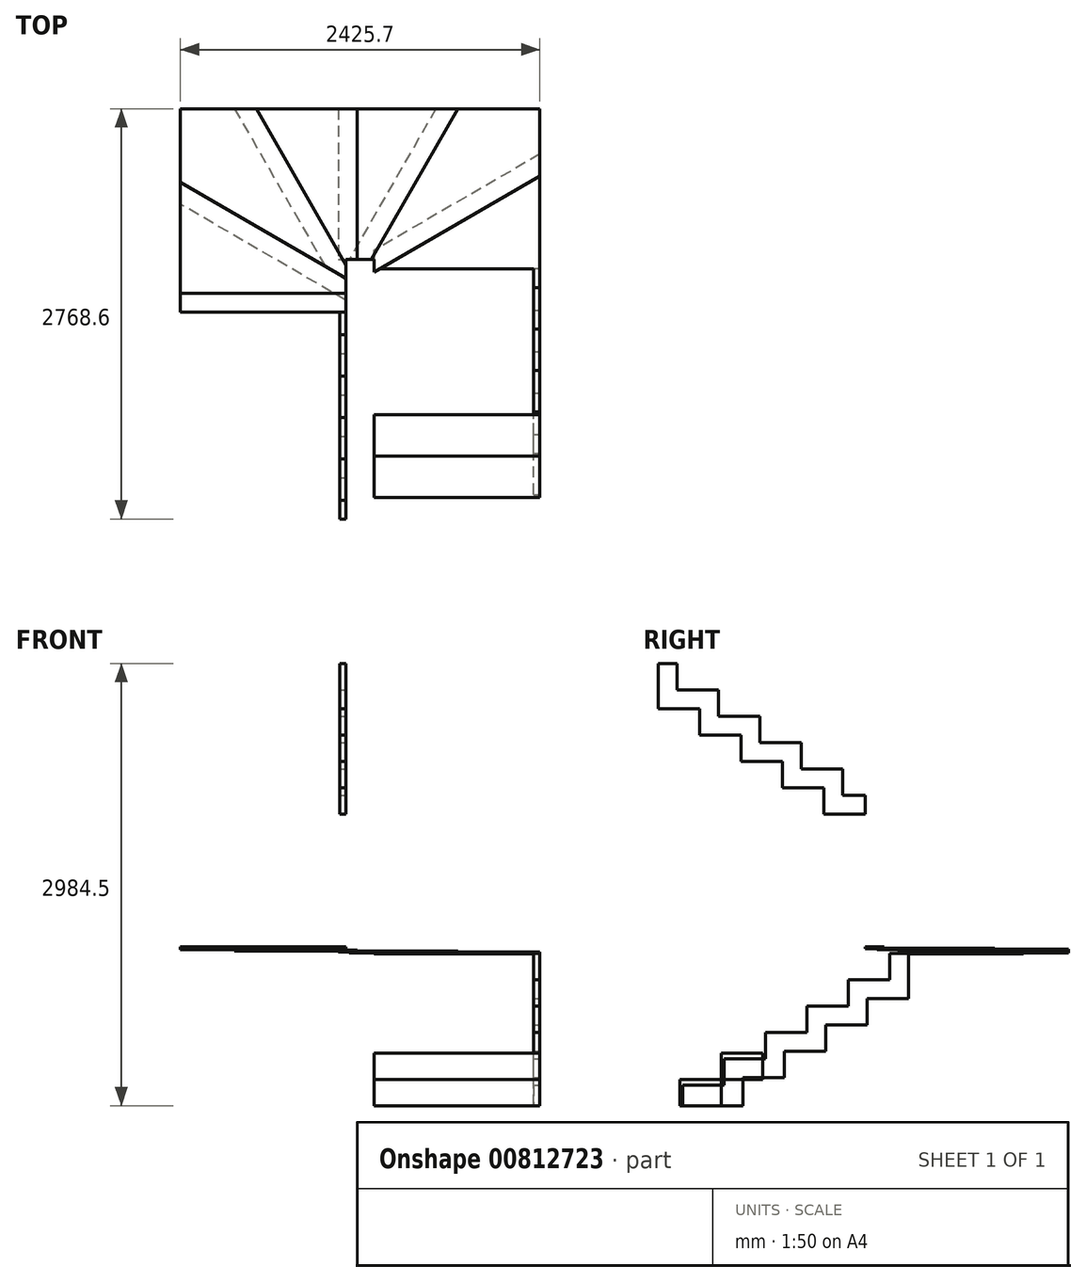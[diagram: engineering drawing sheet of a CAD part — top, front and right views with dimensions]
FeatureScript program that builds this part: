
annotation { "Feature Type Name" : "Feature", "Feature Type Description" : "" }
export const myFeature = defineFeature(function(context is Context, id is Id, definition is map)
    precondition{}
    {
        {
            assignVariable(context, id + "F0", {"name" : "ancho", "anyValue" : 44});
        }
        {
            assignVariable(context, id + "F1", {"name" : "ch", "anyValue" : 7});
        }
        {
            assignVariable(context, id + "F2", {"name" : "tk", "anyValue" : 5});
        }
        {
            var Q0;
            Q0=qCreatedBy(makeId("Top.planeOp"),FACE);
            var sketch = newSketch(context, id + "F3", { "sketchPlane" : qUnion([Q0])});
            skCircle(sketch, "E0", {"center": v(0, 0) * mm, "radius": 1212.85 * mm, "construction": true});
            skLineSegment(sketch, "E1", {"start": v(0, 0) * mm, "end": v(-1212.85, 0) * mm, "construction": true});
            skLineSegment(sketch, "E2", {"start": v(0, 0) * mm, "end": v(1212.85, 0) * mm, "construction": true});
            skLineSegment(sketch, "E3", {"start": v(0, 0) * mm, "end": v(0, 1212.85) * mm, "construction": true});
            skLineSegment(sketch, "E4.bottom", {"start": v(95.25, 1323.25) * mm, "end": v(-95.25, 1323.25) * mm, "construction": true});
            skLineSegment(sketch, "E4.top", {"start": v(95.25, -3517.78) * mm, "end": v(-95.25, -3517.78) * mm, "construction": true});
            skLineSegment(sketch, "E4.left", {"start": v(95.25, 1323.25) * mm, "end": v(95.25, -3517.78) * mm, "construction": true});
            skLineSegment(sketch, "E4.right", {"start": v(-95.25, 1323.25) * mm, "end": v(-95.25, -3517.78) * mm, "construction": true});
            skLineSegment(sketch, "E5", {"start": v(-190.5, 1323.25) * mm, "end": v(-190.5, -3534.77) * mm, "construction": true});
            skLineSegment(sketch, "E6.bottom", {"start": v(-95.25, 0) * mm, "end": v(-1212.85, 0) * mm});
            skLineSegment(sketch, "E6.top", {"start": v(-95.25, -279.4) * mm, "end": v(-1212.85, -279.4) * mm});
            skLineSegment(sketch, "E6.left", {"start": v(-95.25, 0) * mm, "end": v(-95.25, -279.4) * mm});
            skLineSegment(sketch, "E6.right", {"start": v(-1212.85, 0) * mm, "end": v(-1212.85, -279.4) * mm});
            skLineSegment(sketch, "E7", {"start": v(-1212.85, 742.65) * mm, "end": v(73.46, 0) * mm, "construction": true});
            skLineSegment(sketch, "E8", {"start": v(-740.5, 1323.25) * mm, "end": v(623.95, -1040.04) * mm, "construction": true});
            skPoint(sketch, "E9", {"position": v(-190.5, 152.4) * mm});
            skPoint(sketch, "E10", {"position": v(-153.9, 307.25) * mm});
            skLineSegment(sketch, "E11", {"start": v(-153.9, 307.25) * mm, "end": v(0, 307.25) * mm, "construction": true});
            skPoint(sketch, "E12", {"position": v(0, 205.65) * mm});
            skLineSegment(sketch, "E13", {"start": v(0, 205.65) * mm, "end": v(-95.25, 205.65) * mm});
            skPoint(sketch, "E14", {"position": v(-95.25, 205.65) * mm});
            skPoint(sketch, "E15", {"position": v(-95.25, 97.4) * mm});
            skLineSegment(sketch, "E16", {"start": v(-95.25, 0) * mm, "end": v(-95.25, 97.4) * mm});
            skLineSegment(sketch, "E17", {"start": v(-1212.85, 742.65) * mm, "end": v(-1212.85, 0) * mm});
            skLineSegment(sketch, "E18", {"start": v(-1212.85, 742.65) * mm, "end": v(-95.25, 97.4) * mm});
            skLineSegment(sketch, "E19", {"start": v(-95.25, 97.4) * mm, "end": v(-95.25, 205.65) * mm});
            skLineSegment(sketch, "E20", {"start": v(0, 205.65) * mm, "end": v(0, 1323.25) * mm});
            skLineSegment(sketch, "E21", {"start": v(0, 1323.25) * mm, "end": v(-1212.85, 1323.25) * mm});
            skPoint(sketch, "E22", {"position": v(-740.5, 1323.25) * mm});
            skLineSegment(sketch, "E23", {"start": v(-95.25, 205.65) * mm, "end": v(-740.5, 1323.25) * mm});
            skLineSegment(sketch, "E24", {"start": v(-1212.85, 1323.25) * mm, "end": v(-1212.85, 742.65) * mm});
            skSolve(sketch);
        }
        {
            var Q0;
            Q0=qCreatedBy(makeId("Top.planeOp"),FACE);
            var sketch = newSketch(context, id + "F4", { "sketchPlane" : qUnion([Q0])});
            skLineSegment(sketch, "E25.bottom", {"start": v(95.25, 0) * mm, "end": v(1212.85, 0) * mm});
            skLineSegment(sketch, "E25.top", {"start": v(95.25, -279.4) * mm, "end": v(1212.85, -279.4) * mm});
            skLineSegment(sketch, "E25.left", {"start": v(95.25, 0) * mm, "end": v(95.25, -279.4) * mm});
            skLineSegment(sketch, "E25.right", {"start": v(1212.85, 0) * mm, "end": v(1212.85, -279.4) * mm});
            skLineSegment(sketch, "E26", {"start": v(95.25, 0) * mm, "end": v(95.25, 101.6) * mm});
            skLineSegment(sketch, "E27", {"start": v(95.25, 101.6) * mm, "end": v(1212.85, 749.3) * mm});
            skLineSegment(sketch, "E28", {"start": v(1212.85, 749.3) * mm, "end": v(1212.85, 0) * mm});
            skLineSegment(sketch, "E29", {"start": v(190.5, 0) * mm, "end": v(190.5, 156.8) * mm, "construction": true});
            skLineSegment(sketch, "E30", {"start": v(0, 209.55) * mm, "end": v(95.25, 209.55) * mm});
            skLineSegment(sketch, "E31", {"start": v(95.25, 209.55) * mm, "end": v(679.45, 1225.55) * mm});
            skLineSegment(sketch, "E32", {"start": v(679.45, 1225.55) * mm, "end": v(0, 1225.55) * mm});
            skLineSegment(sketch, "E33", {"start": v(0, 1225.55) * mm, "end": v(0, 209.55) * mm});
            skLineSegment(sketch, "E34", {"start": v(679.45, 1225.55) * mm, "end": v(1212.85, 1225.55) * mm});
            skLineSegment(sketch, "E35", {"start": v(1212.85, 1225.55) * mm, "end": v(1212.85, 749.3) * mm});
            skLineSegment(sketch, "E36", {"start": v(0, 304.8) * mm, "end": v(150.02, 304.8) * mm, "construction": true});
            skLineSegment(sketch, "E37", {"start": v(95.25, 209.55) * mm, "end": v(95.25, 101.6) * mm});
            skLineSegment(sketch, "E38", {"start": v(150.02, 304.8) * mm, "end": v(190.5, 304.8) * mm, "construction": true});
            skLineSegment(sketch, "E39", {"start": v(190.5, 304.8) * mm, "end": v(190.5, 156.8) * mm, "construction": true});
            skLineSegment(sketch, "E40", {"start": v(95.25, -279.4) * mm, "end": v(95.25, -558.8) * mm});
            skLineSegment(sketch, "E41", {"start": v(95.25, -558.8) * mm, "end": v(1212.85, -558.8) * mm});
            skLineSegment(sketch, "E42", {"start": v(1212.85, -558.8) * mm, "end": v(1212.85, -279.4) * mm});
            skLineSegment(sketch, "E43", {"start": v(95.25, -558.8) * mm, "end": v(95.25, -838.2) * mm});
            skLineSegment(sketch, "E44", {"start": v(95.25, -838.2) * mm, "end": v(1212.85, -838.2) * mm});
            skLineSegment(sketch, "E45", {"start": v(1212.85, -838.2) * mm, "end": v(1212.85, -558.8) * mm});
            skLineSegment(sketch, "E46", {"start": v(95.25, -838.2) * mm, "end": v(95.25, -1117.6) * mm});
            skLineSegment(sketch, "E47", {"start": v(95.25, -1117.6) * mm, "end": v(1212.85, -1117.6) * mm});
            skLineSegment(sketch, "E48", {"start": v(1212.85, -1117.6) * mm, "end": v(1212.85, -838.2) * mm});
            skLineSegment(sketch, "E49", {"start": v(95.25, -1117.6) * mm, "end": v(95.25, -1397) * mm});
            skLineSegment(sketch, "E50", {"start": v(95.25, -1397) * mm, "end": v(1212.85, -1397) * mm});
            skLineSegment(sketch, "E51", {"start": v(1212.85, -1397) * mm, "end": v(1212.85, -1117.6) * mm});
            skSolve(sketch);
        }
        {
            var Q0;
            Q0=qCreatedBy(makeId("Top.planeOp"),FACE);
            var sketch = newSketch(context, id + "F5", { "sketchPlane" : qUnion([Q0])});
            skLineSegment(sketch, "E52", {"start": v(0, 209.55) * mm, "end": v(-95.25, 209.55) * mm});
            skLineSegment(sketch, "E53", {"start": v(-95.25, 209.55) * mm, "end": v(-679.45, 1225.55) * mm});
            skLineSegment(sketch, "E54", {"start": v(-679.45, 1225.55) * mm, "end": v(0, 1225.55) * mm});
            skLineSegment(sketch, "E55", {"start": v(0, 1225.55) * mm, "end": v(0, 209.55) * mm});
            skLineSegment(sketch, "E56", {"start": v(-679.45, 1225.55) * mm, "end": v(-1212.85, 1225.55) * mm});
            skLineSegment(sketch, "E57", {"start": v(-1212.85, 1225.55) * mm, "end": v(-1212.85, 749.3) * mm});
            skLineSegment(sketch, "E58", {"start": v(-1212.85, 749.3) * mm, "end": v(-95.25, 101.6) * mm});
            skLineSegment(sketch, "E59", {"start": v(-95.25, 101.6) * mm, "end": v(-95.25, 209.55) * mm});
            skLineSegment(sketch, "E60", {"start": v(-95.25, 101.6) * mm, "end": v(-95.25, 0) * mm});
            skLineSegment(sketch, "E61", {"start": v(-95.25, 0) * mm, "end": v(-1212.85, 0) * mm});
            skLineSegment(sketch, "E62", {"start": v(-1212.85, 0) * mm, "end": v(-1212.85, 749.3) * mm});
            skLineSegment(sketch, "E63", {"start": v(-1212.85, 0) * mm, "end": v(-1212.85, -1397) * mm});
            skLineSegment(sketch, "E64", {"start": v(-1212.85, -1397) * mm, "end": v(-95.25, -1397) * mm});
            skLineSegment(sketch, "E65", {"start": v(-95.25, -1397) * mm, "end": v(-95.25, 0) * mm});
            skLineSegment(sketch, "E66", {"start": v(-95.25, -279.4) * mm, "end": v(-1212.85, -279.4) * mm});
            skLineSegment(sketch, "E67", {"start": v(-95.25, -558.8) * mm, "end": v(-1212.85, -558.8) * mm});
            skLineSegment(sketch, "E68", {"start": v(-1212.85, -838.2) * mm, "end": v(-95.25, -838.2) * mm});
            skLineSegment(sketch, "E69", {"start": v(-1212.85, -1117.6) * mm, "end": v(-95.25, -1117.6) * mm});
            skSolve(sketch);
        }
        {
            var Q0;
            Q0=makeQuery(id+"F4.imprint","IMPRINT",FACE,{"disambiguationData":[TD([[makeQuery(id+"F4.imprint","IMPRINT",EDGE,{"derivedFrom":sQuery(id+"F4.wireOp",EDGE,"E47")}),-1.0]])]});
            extrude(context, id + "F6", {"entities" : qUnion([Q0]), "depth" : 177.8 * mm, "offsetDistance" : 25.4 * mm});
        }
        {
            var Q0;
            Q0=makeQuery(id+"F4.imprint","IMPRINT",FACE,{"disambiguationData":[TD([[makeQuery(id+"F4.imprint","IMPRINT",EDGE,{"derivedFrom":sQuery(id+"F4.wireOp",EDGE,"E44")}),-1.0]])]});
            extrude(context, id + "F7", {"entities" : qUnion([Q0]), "depth" : 355.6 * mm, "offsetDistance" : 25.4 * mm, "hasSecondDirection" : true, "secondDirectionOppositeDirection" : true, "secondDirectionDepth" : -177.8 * mm});
        }
        {
            var Q0;
            Q0=makeQuery(id+"F6.opExtrude","SWEPT_FACE",FACE,{"disambiguationData":[OSD([sQuery(id+"F4.wireOp",EDGE,"E51")])]});
            var sketch = newSketch(context, id + "F8", { "sketchPlane" : qUnion([Q0])});
            skLineSegment(sketch, "E70", {"start": v(-1377.95, 139.7) * mm, "end": v(-1377.95, 0) * mm});
            skLineSegment(sketch, "E71", {"start": v(-1098.55, 317.5) * mm, "end": v(-819.15, 317.5) * mm});
            skLineSegment(sketch, "E72", {"start": v(-819.15, 317.5) * mm, "end": v(-819.15, 495.3) * mm});
            skLineSegment(sketch, "E73", {"start": v(-819.15, 495.3) * mm, "end": v(-539.75, 495.3) * mm});
            skLineSegment(sketch, "E74", {"start": v(-539.75, 495.3) * mm, "end": v(-539.75, 673.1) * mm});
            skLineSegment(sketch, "E75", {"start": v(-539.75, 673.1) * mm, "end": v(-260.35, 673.1) * mm});
            skLineSegment(sketch, "E76", {"start": v(-260.35, 673.1) * mm, "end": v(-260.35, 850.9) * mm});
            skLineSegment(sketch, "E77", {"start": v(-260.35, 850.9) * mm, "end": v(19.05, 850.9) * mm});
            skLineSegment(sketch, "E78", {"start": v(-971.55, 0) * mm, "end": v(-971.55, 190.5) * mm});
            skLineSegment(sketch, "E79", {"start": v(-971.55, 190.5) * mm, "end": v(-692.15, 190.5) * mm});
            skLineSegment(sketch, "E80", {"start": v(-692.15, 190.5) * mm, "end": v(-692.15, 368.3) * mm});
            skLineSegment(sketch, "E81", {"start": v(-692.15, 368.3) * mm, "end": v(-412.75, 368.3) * mm});
            skLineSegment(sketch, "E82", {"start": v(-412.75, 368.3) * mm, "end": v(-412.75, 546.1) * mm});
            skLineSegment(sketch, "E83", {"start": v(-412.75, 546.1) * mm, "end": v(-133.35, 546.1) * mm});
            skLineSegment(sketch, "E84", {"start": v(-133.35, 546.1) * mm, "end": v(-133.35, 723.9) * mm});
            skLineSegment(sketch, "E85", {"start": v(-133.35, 723.9) * mm, "end": v(146.05, 723.9) * mm});
            skLineSegment(sketch, "E86", {"start": v(-1377.95, 0) * mm, "end": v(-971.55, 0) * mm});
            skLineSegment(sketch, "E87", {"start": v(-1377.95, 139.7) * mm, "end": v(-1098.55, 139.7) * mm});
            skLineSegment(sketch, "E88", {"start": v(-1098.55, 139.7) * mm, "end": v(-1098.55, 317.5) * mm});
            skLineSegment(sketch, "E89", {"start": v(19.05, 850.9) * mm, "end": v(19.05, 1028.7) * mm});
            skLineSegment(sketch, "E90", {"start": v(19.05, 1028.7) * mm, "end": v(146.05, 1028.7) * mm});
            skLineSegment(sketch, "E91", {"start": v(146.05, 723.9) * mm, "end": v(146.05, 1028.7) * mm});
            skSolve(sketch);
        }
        {
            var Q0;
            {var subQ4=sQuery(id+"F8.wireOp",EDGE,"E71");Q0=makeQuery(id+"F8.imprint","IMPRINT",FACE,{"disambiguationData":[TD([[makeQuery(id+"F8.imprint","IMPRINT",EDGE,{"derivedFrom":subQ4}),-1.0]])]});}
            var Q1;
            {var subQ1=sQuery(id+"F8.wireOp",EDGE,"RiLGjqe3-f55V-vZne-o9eZ-Tra6b2igqHXF.right");Q1=makeQuery(id+"F8.imprint","IMPRINT",FACE,{"disambiguationData":[TD([[makeQuery(id+"F8.imprint","IMPRINT",EDGE,{"derivedFrom":subQ1}),1.0]])]});}
            var Q2;
            {var subQ0=sQuery(id+"F8.wireOp",EDGE,"E70");Q2=makeQuery(id+"F8.imprint","IMPRINT",FACE,{"disambiguationData":[TD([[makeQuery(id+"F8.imprint","IMPRINT",EDGE,{"derivedFrom":subQ0}),1.0]])]});}
            extrude(context, id + "F9", {"entities" : qUnion([Q0, Q1, Q2]), "oppositeDirection" : true, "depth" : (getVariable(context, 'ancho')) * mm, "offsetDistance" : 25.4 * mm});
        }
        {
            var Q0;
            Q0=makeQuery(id+"F9.opExtrude","SWEPT_FACE",FACE,{"disambiguationData":[OSD([sQuery(id+"F8.wireOp",EDGE,"E90")])]});
            var sketch = newSketch(context, id + "F10", { "sketchPlane" : qUnion([Q0])});
            skLineSegment(sketch, "E92", {"start": v(95.25, 123.62) * mm, "end": v(1212.85, 771.32) * mm});
            skLineSegment(sketch, "E93", {"start": v(1212.85, 918.1) * mm, "end": v(-9.75, 209.55) * mm});
            skLineSegment(sketch, "E94", {"start": v(95.25, 123.62) * mm, "end": v(95.25, 209.55) * mm});
            skLineSegment(sketch, "E95", {"start": v(95.25, 209.55) * mm, "end": v(-9.75, 209.55) * mm});
            skLineSegment(sketch, "E96", {"start": v(1212.85, 918.1) * mm, "end": v(1212.85, 771.32) * mm});
            skLineSegment(sketch, "E97", {"start": v(1212.85, 771.32) * mm, "end": v(1212.85, 146.05) * mm});
            skLineSegment(sketch, "E98", {"start": v(1212.85, 146.05) * mm, "end": v(133.96, 146.05) * mm});
            skLineSegment(sketch, "E99", {"start": v(133.96, 146.05) * mm, "end": v(1212.85, 771.32) * mm});
            skSolve(sketch);
        }
        {
            var Q0;
            Q0=makeQuery(id+"F10.imprint","IMPRINT",FACE,{"disambiguationData":[TD([[makeQuery(id+"F10.imprint","IMPRINT",EDGE,{"derivedFrom":sQuery(id+"F10.wireOp",EDGE,"E97")}),-1.0]])]});
            extrude(context, id + "F11", {"entities" : qUnion([Q0]), "operationType" : NewBodyOperationType.ADD, "oppositeDirection" : true, "depth" : (getVariable(context, 'tk')) * mm, "offsetDistance" : 25.4 * mm});
        }
        {
            var Q0;
            Q0=makeQuery(id+"F10.imprint","IMPRINT",FACE,{"disambiguationData":[TD([[makeQuery(id+"F10.imprint","IMPRINT",EDGE,{"derivedFrom":sQuery(id+"F10.wireOp",EDGE,"E93")}),1.0]])]});
            var Q1;
            {var subQ0=sQuery(id+"F10.wireOp",EDGE,"E92");Q1=makeQuery(id+"F10.imprint","IMPRINT",FACE,{"disambiguationData":[TD([[makeQuery(id+"F10.imprint","IMPRINT",EDGE,{"derivedFrom":subQ0}),1.0]])]});}
            extrude(context, id + "F12", {"entities" : qUnion([Q0, Q1]), "operationType" : NewBodyOperationType.ADD, "depth" : (getVariable(context, 'ch')) * mm, "offsetDistance" : 25.4 * mm, "hasSecondDirection" : true, "secondDirectionOppositeDirection" : true, "secondDirectionDepth" : (getVariable(context, 'tk')) * mm});
        }
        {
            var Q0;
            Q0=makeQuery(id+"F12.opExtrude","CAP_FACE",FACE,{"disambiguationData":[OSD([sQuery(id+"F10.wireOp",EDGE,"E92"),sQuery(id+"F10.wireOp",EDGE,"E93"),sQuery(id+"F10.wireOp",EDGE,"E94"),sQuery(id+"F10.wireOp",EDGE,"E95"),sQuery(id+"F10.wireOp",EDGE,"E96"),sQuery(id+"F10.wireOp",EDGE,"E99")])],"isStart":false});
            var sketch = newSketch(context, id + "F13", { "sketchPlane" : qUnion([Q0])});
            skLineSegment(sketch, "E100", {"start": v(510.98, 1225.55) * mm, "end": v(-73.22, 209.55) * mm});
            skLineSegment(sketch, "E101", {"start": v(657.48, 1225.55) * mm, "end": v(73.28, 209.55) * mm});
            skLineSegment(sketch, "E102", {"start": v(-73.22, 209.55) * mm, "end": v(73.28, 209.55) * mm});
            skLineSegment(sketch, "E103", {"start": v(510.98, 1225.55) * mm, "end": v(657.48, 1225.55) * mm});
            skLineSegment(sketch, "E104", {"start": v(657.48, 1225.55) * mm, "end": v(1212.85, 1225.55) * mm});
            skLineSegment(sketch, "E105", {"start": v(1212.85, 1225.55) * mm, "end": v(1212.85, 918.1) * mm});
            skLineSegment(sketch, "E106", {"start": v(1212.85, 918.1) * mm, "end": v(114.77, 281.72) * mm});
            skSolve(sketch);
        }
        {
            var Q0;
            {var subQ0=sQuery(id+"F13.wireOp",EDGE,"E104");Q0=makeQuery(id+"F13.imprint","IMPRINT",FACE,{"disambiguationData":[TD([[makeQuery(id+"F13.imprint","IMPRINT",EDGE,{"derivedFrom":subQ0}),-1.0]])]});}
            extrude(context, id + "F14", {"entities" : qUnion([Q0]), "operationType" : NewBodyOperationType.ADD, "oppositeDirection" : true, "depth" : (getVariable(context, 'tk')) * mm, "offsetDistance" : 25.4 * mm});
        }
        {
            var Q0;
            {var subQ3=sQuery(id+"F13.wireOp",EDGE,"E100");Q0=makeQuery(id+"F13.imprint","IMPRINT",FACE,{"disambiguationData":[TD([[makeQuery(id+"F13.imprint","IMPRINT",EDGE,{"derivedFrom":subQ3}),1.0]])]});}
            var Q1;
            {var subQ0=sQuery(id+"F13.wireOp",EDGE,"E102");var subQ1=sQuery(id+"F13.wireOp",EDGE,"E101");var subQ2=makeQuery(id+"F13.imprint","INTERSECT",VERTEX,{"derivedFrom":[makeQuery(id+"F12.opExtrude","CAP_EDGE",EDGE,{"disambiguationData":[OSD([sQuery(id+"F10.wireOp",EDGE,"E95")])],"isStart":false}),subQ1,subQ0]});Q1=makeQuery(id+"F13.imprint","IMPRINT",FACE,{"disambiguationData":[TD([[makeQuery(id+"F13.imprint","IMPRINT",EDGE,{"disambiguationData":[TD([[subQ2,-1.0]])],"derivedFrom":subQ0}),-1.0]])]});}
            extrude(context, id + "F15", {"entities" : qUnion([Q0, Q1]), "operationType" : NewBodyOperationType.ADD, "depth" : (getVariable(context, 'ch')) * mm, "offsetDistance" : 25.4 * mm, "hasSecondDirection" : true, "secondDirectionOppositeDirection" : true, "secondDirectionDepth" : (getVariable(context, 'tk')) * mm});
        }
        {
            var Q0;
            Q0=makeQuery(id+"F15.opExtrude","CAP_FACE",FACE,{"disambiguationData":[OSD([sQuery(id+"F13.wireOp",EDGE,"E100"),sQuery(id+"F13.wireOp",EDGE,"E101"),sQuery(id+"F13.wireOp",EDGE,"E102"),sQuery(id+"F13.wireOp",EDGE,"E103")])],"isStart":false});
            var sketch = newSketch(context, id + "F16", { "sketchPlane" : qUnion([Q0])});
            skLineSegment(sketch, "E107", {"start": v(-146.05, 1225.55) * mm, "end": v(-146.05, 209.55) * mm});
            skLineSegment(sketch, "E108", {"start": v(-146.05, 209.55) * mm, "end": v(-19.05, 209.55) * mm});
            skLineSegment(sketch, "E109", {"start": v(-19.05, 1225.55) * mm, "end": v(-19.05, 209.55) * mm});
            skLineSegment(sketch, "E110", {"start": v(510.98, 1225.55) * mm, "end": v(-19.05, 303.76) * mm});
            skLineSegment(sketch, "E111", {"start": v(-146.05, 1225.55) * mm, "end": v(-19.05, 1225.55) * mm});
            skLineSegment(sketch, "E112", {"start": v(-19.05, 1225.55) * mm, "end": v(510.98, 1225.55) * mm});
            skSolve(sketch);
        }
        {
            var Q0;
            {var subQ2=sQuery(id+"F16.wireOp",EDGE,"E110");Q0=makeQuery(id+"F16.imprint","IMPRINT",FACE,{"disambiguationData":[TD([[makeQuery(id+"F16.imprint","IMPRINT",EDGE,{"derivedFrom":subQ2}),-1.0]])]});}
            extrude(context, id + "F17", {"entities" : qUnion([Q0]), "operationType" : NewBodyOperationType.ADD, "oppositeDirection" : true, "depth" : (getVariable(context, 'tk')) * mm, "offsetDistance" : 25.4 * mm});
        }
        {
            var Q0;
            {var subQ6=sQuery(id+"F16.wireOp",EDGE,"E107");Q0=makeQuery(id+"F16.imprint","IMPRINT",FACE,{"disambiguationData":[TD([[makeQuery(id+"F16.imprint","IMPRINT",EDGE,{"derivedFrom":subQ6}),1.0]])]});}
            var Q1;
            {var subQ0=sQuery(id+"F16.wireOp",EDGE,"E108");var subQ1=makeQuery(id+"F15.opExtrude","CAP_EDGE",EDGE,{"disambiguationData":[OSD([sQuery(id+"F13.wireOp",EDGE,"E100")])],"isStart":false});var subQ2=makeQuery(id+"F16.imprint","INTERSECT",VERTEX,{"derivedFrom":[subQ1,subQ0]});Q1=makeQuery(id+"F16.imprint","IMPRINT",FACE,{"disambiguationData":[TD([[makeQuery(id+"F16.imprint","IMPRINT",EDGE,{"disambiguationData":[TD([[subQ2,-1.0]])],"derivedFrom":subQ0}),1.0]])]});}
            extrude(context, id + "F18", {"entities" : qUnion([Q0, Q1]), "operationType" : NewBodyOperationType.ADD, "depth" : (getVariable(context, 'ch')) * mm, "offsetDistance" : 25.4 * mm, "hasSecondDirection" : true, "secondDirectionOppositeDirection" : true, "secondDirectionDepth" : (getVariable(context, 'tk')) * mm});
        }
        {
            var Q0;
            Q0=makeQuery(id+"F18.opExtrude","CAP_FACE",FACE,{"disambiguationData":[OSD([sQuery(id+"F16.wireOp",EDGE,"E107"),sQuery(id+"F16.wireOp",EDGE,"E108"),sQuery(id+"F16.wireOp",EDGE,"E109"),sQuery(id+"F16.wireOp",EDGE,"E111")])],"isStart":false});
            var sketch = newSketch(context, id + "F19", { "sketchPlane" : qUnion([Q0])});
            skLineSegment(sketch, "E113", {"start": v(-701.42, 1225.55) * mm, "end": v(-95.25, 171.33) * mm});
            skLineSegment(sketch, "E114", {"start": v(-847.92, 1225.55) * mm, "end": v(-95.25, -83.45) * mm});
            skLineSegment(sketch, "E115", {"start": v(-847.92, 1225.55) * mm, "end": v(-701.42, 1225.55) * mm});
            skLineSegment(sketch, "E116", {"start": v(-701.42, 1225.55) * mm, "end": v(-146.05, 1225.55) * mm});
            skLineSegment(sketch, "E117", {"start": v(-146.05, 1225.55) * mm, "end": v(-146.05, 259.68) * mm});
            skLineSegment(sketch, "E118", {"start": v(-95.25, 171.33) * mm, "end": v(-95.25, -83.45) * mm});
            skLineSegment(sketch, "E119", {"start": v(-95.25, 171.33) * mm, "end": v(-95.25, 209.55) * mm});
            skLineSegment(sketch, "E120", {"start": v(-229.51, 150.05) * mm, "end": v(-95.25, 72.24) * mm});
            skSolve(sketch);
        }
        {
            var Q0;
            {var subQ0=sQuery(id+"F19.wireOp",EDGE,"E116");Q0=makeQuery(id+"F19.imprint","IMPRINT",FACE,{"disambiguationData":[TD([[makeQuery(id+"F19.imprint","IMPRINT",EDGE,{"derivedFrom":subQ0}),-1.0]])]});}
            var Q1;
            {var subQ0=sQuery(id+"F19.wireOp",EDGE,"E119");Q1=makeQuery(id+"F19.imprint","IMPRINT",FACE,{"disambiguationData":[TD([[makeQuery(id+"F19.imprint","IMPRINT",EDGE,{"derivedFrom":subQ0}),1.0]])]});}
            extrude(context, id + "F20", {"entities" : qUnion([Q0, Q1]), "operationType" : NewBodyOperationType.ADD, "oppositeDirection" : true, "depth" : (getVariable(context, 'tk')) * mm, "offsetDistance" : 25.4 * mm});
        }
        {
            var Q0;
            {var subQ0=sQuery(id+"F19.wireOp",EDGE,"E115");Q0=makeQuery(id+"F19.imprint","IMPRINT",FACE,{"disambiguationData":[TD([[makeQuery(id+"F19.imprint","IMPRINT",EDGE,{"derivedFrom":subQ0}),-1.0]])]});}
            var Q1;
            {var subQ1=makeQuery(id+"F18.opExtrude","CAP_EDGE",EDGE,{"disambiguationData":[OSD([sQuery(id+"F16.wireOp",EDGE,"E107")])],"isStart":false});var subQ3=makeQuery(id+"F18.opExtrude","CAP_EDGE",EDGE,{"disambiguationData":[OSD([sQuery(id+"F16.wireOp",EDGE,"E108")])],"isStart":false});var subQ5=makeQuery(id+"F19.imprint","INTERSECT",VERTEX,{"derivedFrom":[subQ1,subQ3]});Q1=makeQuery(id+"F19.imprint","IMPRINT",FACE,{"disambiguationData":[TD([[makeQuery(id+"F19.imprint","IMPRINT",EDGE,{"disambiguationData":[TD([[subQ5,-1.0]])],"derivedFrom":subQ3}),1.0]])]});}
            extrude(context, id + "F21", {"entities" : qUnion([Q0, Q1]), "operationType" : NewBodyOperationType.ADD, "depth" : (getVariable(context, 'ch')) * mm, "offsetDistance" : 25.4 * mm, "hasSecondDirection" : true, "secondDirectionOppositeDirection" : true, "secondDirectionDepth" : (getVariable(context, 'tk')) * mm});
        }
        {
            var Q0;
            Q0=makeQuery(id+"F21.opExtrude","CAP_FACE",FACE,{"disambiguationData":[OSD([sQuery(id+"F19.wireOp",EDGE,"E113"),sQuery(id+"F19.wireOp",EDGE,"E114"),sQuery(id+"F19.wireOp",EDGE,"E115"),sQuery(id+"F19.wireOp",EDGE,"E118")])],"isStart":false});
            var sketch = newSketch(context, id + "F22", { "sketchPlane" : qUnion([Q0])});
            skLineSegment(sketch, "E121", {"start": v(-847.92, 1225.55) * mm, "end": v(-235.84, 161.06) * mm});
            skLineSegment(sketch, "E122", {"start": v(-1212.85, 727.28) * mm, "end": v(-95.25, 79.58) * mm});
            skLineSegment(sketch, "E123", {"start": v(-95.25, 79.58) * mm, "end": v(-95.25, -67.2) * mm});
            skLineSegment(sketch, "E124", {"start": v(-95.25, -67.2) * mm, "end": v(-1212.85, 580.5) * mm});
            skLineSegment(sketch, "E125", {"start": v(-1212.85, 580.5) * mm, "end": v(-1212.85, 727.28) * mm});
            skLineSegment(sketch, "E126", {"start": v(-1212.85, 727.28) * mm, "end": v(-1212.85, 1225.55) * mm});
            skLineSegment(sketch, "E127", {"start": v(-1212.85, 1225.55) * mm, "end": v(-847.92, 1225.55) * mm});
            skSolve(sketch);
        }
        {
            var Q0;
            {var subQ0=sQuery(id+"F22.wireOp",EDGE,"E121");Q0=makeQuery(id+"F22.imprint","IMPRINT",FACE,{"disambiguationData":[TD([[makeQuery(id+"F22.imprint","IMPRINT",EDGE,{"derivedFrom":subQ0}),-1.0]])]});}
            extrude(context, id + "F23", {"entities" : qUnion([Q0]), "operationType" : NewBodyOperationType.ADD, "oppositeDirection" : true, "depth" : (getVariable(context, 'tk')) * mm, "offsetDistance" : 25.4 * mm});
        }
        {
            var Q0;
            {var subQ3=sQuery(id+"F22.wireOp",EDGE,"E125");Q0=makeQuery(id+"F22.imprint","IMPRINT",FACE,{"disambiguationData":[TD([[makeQuery(id+"F22.imprint","IMPRINT",EDGE,{"derivedFrom":subQ3}),-1.0]])]});}
            var Q1;
            {var subQ3=sQuery(id+"F22.wireOp",EDGE,"E123");Q1=makeQuery(id+"F22.imprint","IMPRINT",FACE,{"disambiguationData":[TD([[makeQuery(id+"F22.imprint","IMPRINT",EDGE,{"derivedFrom":subQ3}),-1.0]])]});}
            extrude(context, id + "F24", {"entities" : qUnion([Q0, Q1]), "operationType" : NewBodyOperationType.ADD, "depth" : (getVariable(context, 'ch')) * mm, "offsetDistance" : 25.4 * mm, "hasSecondDirection" : true, "secondDirectionOppositeDirection" : true, "secondDirectionDepth" : (getVariable(context, 'tk')) * mm});
        }
        {
            var Q0;
            Q0=makeQuery(id+"F24.opExtrude","CAP_FACE",FACE,{"disambiguationData":[OSD([sQuery(id+"F22.wireOp",EDGE,"E122"),sQuery(id+"F22.wireOp",EDGE,"E123"),sQuery(id+"F22.wireOp",EDGE,"E124"),sQuery(id+"F22.wireOp",EDGE,"E125")])],"isStart":false});
            var sketch = newSketch(context, id + "F25", { "sketchPlane" : qUnion([Q0])});
            skLineSegment(sketch, "E128", {"start": v(-1212.85, 580.5) * mm, "end": v(-1212.85, -19.05) * mm});
            skLineSegment(sketch, "E129", {"start": v(-1212.85, -19.05) * mm, "end": v(-95.25, -19.05) * mm});
            skLineSegment(sketch, "E130", {"start": v(-95.25, -19.05) * mm, "end": v(-95.25, -146.05) * mm});
            skLineSegment(sketch, "E131", {"start": v(-95.25, -146.05) * mm, "end": v(-1212.85, -146.05) * mm});
            skLineSegment(sketch, "E132", {"start": v(-1212.85, -146.05) * mm, "end": v(-1212.85, -19.05) * mm});
            skLineSegment(sketch, "E133", {"start": v(-1212.85, 580.5) * mm, "end": v(-178.34, -19.05) * mm});
            skSolve(sketch);
        }
        {
            var Q0;
            {var subQ0=sQuery(id+"F25.wireOp",EDGE,"E128");Q0=makeQuery(id+"F25.imprint","IMPRINT",FACE,{"disambiguationData":[TD([[makeQuery(id+"F25.imprint","IMPRINT",EDGE,{"derivedFrom":subQ0}),1.0]])]});}
            extrude(context, id + "F26", {"entities" : qUnion([Q0]), "operationType" : NewBodyOperationType.ADD, "oppositeDirection" : true, "depth" : (getVariable(context, 'tk')) * mm, "offsetDistance" : 25.4 * mm});
        }
        {
            var Q0;
            {var subQ0=sQuery(id+"F25.wireOp",EDGE,"E131");Q0=makeQuery(id+"F25.imprint","IMPRINT",FACE,{"disambiguationData":[TD([[makeQuery(id+"F25.imprint","IMPRINT",EDGE,{"derivedFrom":subQ0}),-1.0]])]});}
            var Q1;
            {var subQ0=sQuery(id+"F25.wireOp",EDGE,"E130");var subQ3=makeQuery(id+"F24.opExtrude","CAP_EDGE",EDGE,{"disambiguationData":[OSD([sQuery(id+"F22.wireOp",EDGE,"E124")])],"isStart":false});var subQ5=makeQuery(id+"F25.imprint","INTERSECT",VERTEX,{"derivedFrom":[subQ3,subQ0]});Q1=makeQuery(id+"F25.imprint","IMPRINT",FACE,{"disambiguationData":[TD([[makeQuery(id+"F25.imprint","IMPRINT",EDGE,{"disambiguationData":[TD([[subQ5,1.0]])],"derivedFrom":subQ0}),-1.0]])]});}
            extrude(context, id + "F27", {"entities" : qUnion([Q0, Q1]), "operationType" : NewBodyOperationType.ADD, "depth" : (getVariable(context, 'ch')) * mm, "offsetDistance" : 25.4 * mm, "hasSecondDirection" : true, "secondDirectionOppositeDirection" : true, "secondDirectionDepth" : (getVariable(context, 'tk')) * mm});
        }
        {
            var Q0;
            Q0=makeQuery(id+"F27.boolean.opBoolean","MERGE",FACE,{"derivedFrom":[makeQuery(id+"F24.boolean.opBoolean","MERGE",FACE,{"derivedFrom":[makeQuery(id+"F21.boolean.opBoolean","MERGE",FACE,{"derivedFrom":[makeQuery(id+"F20.opExtrude","SWEPT_FACE",FACE,{"disambiguationData":[OSD([sQuery(id+"F19.wireOp",EDGE,"E119")])]}),makeQuery(id+"F21.opExtrude","SWEPT_FACE",FACE,{"disambiguationData":[OSD([sQuery(id+"F19.wireOp",EDGE,"E118")])]})]}),makeQuery(id+"F24.opExtrude","SWEPT_FACE",FACE,{"disambiguationData":[OSD([sQuery(id+"F22.wireOp",EDGE,"E123")])]})]}),makeQuery(id+"F27.opExtrude","SWEPT_FACE",FACE,{"disambiguationData":[OSD([sQuery(id+"F25.wireOp",EDGE,"E130")])]})]});
            var sketch = newSketch(context, id + "F28", { "sketchPlane" : qUnion([Q0])});
            skLineSegment(sketch, "E134", {"start": v(-146.05, 2095.5) * mm, "end": v(-298.45, 2095.5) * mm});
            skLineSegment(sketch, "E135", {"start": v(-298.45, 2095.5) * mm, "end": v(-298.45, 2273.3) * mm});
            skLineSegment(sketch, "E136", {"start": v(-298.45, 2273.3) * mm, "end": v(-577.85, 2273.3) * mm});
            skLineSegment(sketch, "E137", {"start": v(-577.85, 2273.3) * mm, "end": v(-577.85, 2451.1) * mm});
            skLineSegment(sketch, "E138", {"start": v(-577.85, 2451.1) * mm, "end": v(-857.25, 2451.1) * mm});
            skLineSegment(sketch, "E139", {"start": v(-857.25, 2451.1) * mm, "end": v(-857.25, 2628.9) * mm});
            skLineSegment(sketch, "E140", {"start": v(-857.25, 2628.9) * mm, "end": v(-1136.65, 2628.9) * mm});
            skLineSegment(sketch, "E141", {"start": v(-1136.65, 2628.9) * mm, "end": v(-1136.65, 2806.7) * mm});
            skLineSegment(sketch, "E142", {"start": v(-1136.65, 2806.7) * mm, "end": v(-1416.05, 2806.7) * mm});
            skLineSegment(sketch, "E143", {"start": v(-146.05, 2095.5) * mm, "end": v(-146.05, 1968.5) * mm});
            skPoint(sketch, "E143.endSnap0", {"position": v(-146.05, 1943.1) * mm});
            skLineSegment(sketch, "E144", {"start": v(-146.05, 1968.5) * mm, "end": v(-425.45, 1968.5) * mm});
            skLineSegment(sketch, "E145", {"start": v(-425.45, 1968.5) * mm, "end": v(-425.45, 2146.3) * mm});
            skLineSegment(sketch, "E146", {"start": v(-425.45, 2146.3) * mm, "end": v(-704.85, 2146.3) * mm});
            skLineSegment(sketch, "E147", {"start": v(-704.85, 2146.3) * mm, "end": v(-704.85, 2324.1) * mm});
            skLineSegment(sketch, "E148", {"start": v(-704.85, 2324.1) * mm, "end": v(-984.25, 2324.1) * mm});
            skLineSegment(sketch, "E149", {"start": v(-984.25, 2324.1) * mm, "end": v(-984.25, 2501.9) * mm});
            skLineSegment(sketch, "E150", {"start": v(-984.25, 2501.9) * mm, "end": v(-1263.65, 2501.9) * mm});
            skLineSegment(sketch, "E151", {"start": v(-1416.05, 2806.7) * mm, "end": v(-1416.05, 2984.5) * mm});
            skLineSegment(sketch, "E152", {"start": v(-1416.05, 2984.5) * mm, "end": v(-1543.05, 2984.5) * mm});
            skLineSegment(sketch, "E153", {"start": v(-1543.05, 2984.5) * mm, "end": v(-1543.05, 2679.7) * mm});
            skLineSegment(sketch, "E154", {"start": v(-1263.65, 2501.9) * mm, "end": v(-1263.65, 2679.7) * mm});
            skLineSegment(sketch, "E155", {"start": v(-1263.65, 2679.7) * mm, "end": v(-1543.05, 2679.7) * mm});
            skSolve(sketch);
        }
        {
            var Q0;
            Q0=makeQuery(id+"F28.imprint","IMPRINT",FACE,{"disambiguationData":[TD([[makeQuery(id+"F28.imprint","IMPRINT",EDGE,{"derivedFrom":sQuery(id+"F28.wireOp",EDGE,"E134")}),1.0]])]});
            extrude(context, id + "F29", {"entities" : qUnion([Q0]), "operationType" : NewBodyOperationType.ADD, "oppositeDirection" : true, "depth" : (getVariable(context, 'ancho')) * mm, "offsetDistance" : 25.4 * mm});
        }
        {
            var Q0;
            {var subQ0=sQuery(id+"F10.wireOp",EDGE,"E99");Q0=makeQuery(id+"F12.boolean.opBoolean","MERGE",FACE,{"derivedFrom":[makeQuery(id+"F11.opExtrude","CAP_FACE",FACE,{"disambiguationData":[OSD([sQuery(id+"F10.wireOp",EDGE,"E97"),sQuery(id+"F10.wireOp",EDGE,"E98"),subQ0])],"isStart":false}),makeQuery(id+"F12.opExtrude","CAP_FACE",FACE,{"disambiguationData":[OSD([sQuery(id+"F10.wireOp",EDGE,"E92"),sQuery(id+"F10.wireOp",EDGE,"E93"),sQuery(id+"F10.wireOp",EDGE,"E94"),sQuery(id+"F10.wireOp",EDGE,"E95"),sQuery(id+"F10.wireOp",EDGE,"E96"),subQ0])],"isStart":true})]});}
            var sketch = newSketch(context, id + "F30", { "sketchPlane" : qUnion([Q0])});
            skLineSegment(sketch, "E156.bottom", {"start": v(95.25, -209.55) * mm, "end": v(-9.75, -209.55) * mm});
            skLineSegment(sketch, "E156.top", {"start": v(95.25, -144.17) * mm, "end": v(-9.75, -144.17) * mm});
            skLineSegment(sketch, "E156.left", {"start": v(95.25, -209.55) * mm, "end": v(95.25, -144.17) * mm});
            skLineSegment(sketch, "E156.right", {"start": v(-9.75, -209.55) * mm, "end": v(-9.75, -144.17) * mm});
            skLineSegment(sketch, "E157", {"start": v(-9.75, -209.55) * mm, "end": v(95.25, -270.4) * mm});
            skLineSegment(sketch, "E158", {"start": v(95.25, -270.4) * mm, "end": v(95.25, -209.55) * mm});
            skSolve(sketch);
        }
        {
            var Q0;
            Q0=makeQuery(id+"F30.imprint","IMPRINT",FACE,{"disambiguationData":[TD([[makeQuery(id+"F30.imprint","IMPRINT",EDGE,{"derivedFrom":sQuery(id+"F30.wireOp",EDGE,"E156.bottom")}),1.0]])]});
            extrude(context, id + "F31", {"entities" : qUnion([Q0]), "operationType" : NewBodyOperationType.REMOVE, "oppositeDirection" : true, "depth" : (getVariable(context, 'ch')) * mm, "offsetDistance" : 25.4 * mm});
        }
    });
